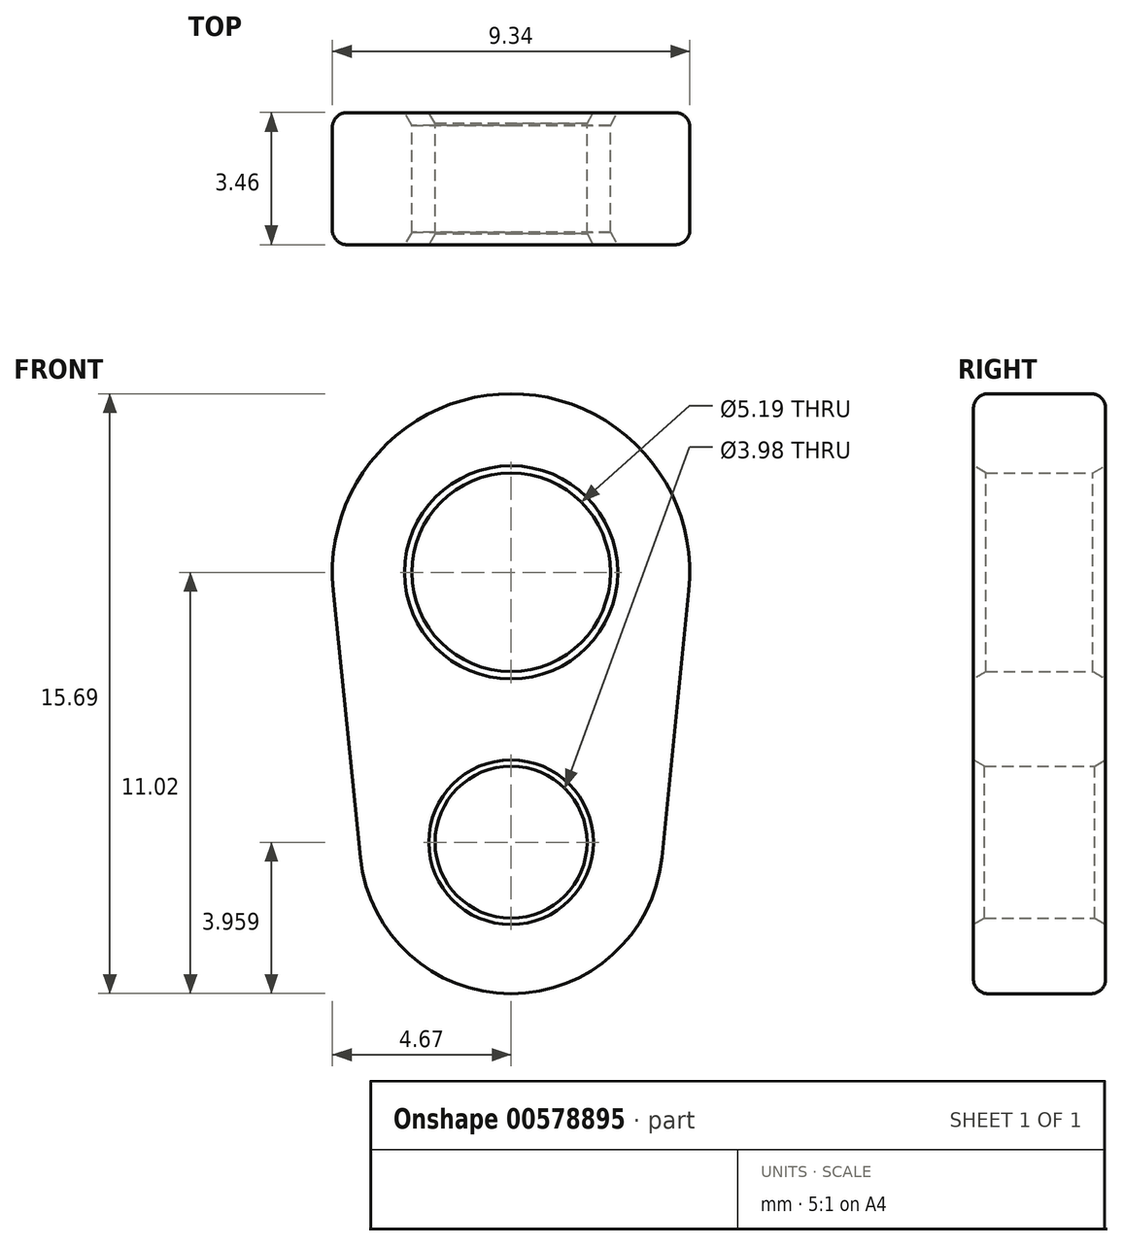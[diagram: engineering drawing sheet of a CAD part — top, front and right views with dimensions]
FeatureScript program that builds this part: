
annotation { "Feature Type Name" : "Feature", "Feature Type Description" : "" }
export const myFeature = defineFeature(function(context is Context, id is Id, definition is map)
    precondition{}
    {
        {
            var Q0;
            Q0=qCreatedBy(makeId("Front.planeOp"),FACE);
            var sketch = newSketch(context, id + "F0", { "sketchPlane" : qUnion([Q0])});
            skCircle(sketch, "E0", {"center": v(0, 0) * mm, "radius": 2.6 * mm});
            skCircle(sketch, "E1", {"center": v(0, -7.06) * mm, "radius": 1.99 * mm});
            skArc(sketch, "E2", {"start": v(-4.65, -0.47) * mm, "mid": v(0, 4.67) * mm, "end": v(4.65, -0.47) * mm});
            skArc(sketch, "E3", {"start": v(-3.94, -7.46) * mm, "mid": v(0, -11.02) * mm, "end": v(3.94, -7.46) * mm});
            skLineSegment(sketch, "E4", {"start": v(-4.65, -0.47) * mm, "end": v(-3.94, -7.46) * mm});
            skLineSegment(sketch, "E5", {"start": v(4.65, -0.47) * mm, "end": v(3.94, -7.46) * mm});
            skSolve(sketch);
        }
        {
            var Q0;
            Q0=makeQuery(id+"F0.imprint","IMPRINT",FACE,{"disambiguationData":[TD([[makeQuery(id+"F0.imprint","IMPRINT",EDGE,{"derivedFrom":sQuery(id+"F0.wireOp",EDGE,"E0")}),-1.0]])]});
            extrude(context, id + "F1", {"entities" : qUnion([Q0]), "endBound" : BoundingType.SYMMETRIC, "depth" : 3.45 * mm});
        }
        {
            var Q0;
            Q0=makeQuery(id+"F1.opExtrude","CAP_EDGE",EDGE,{"disambiguationData":[OSD([sQuery(id+"F0.wireOp",EDGE,"E5")])],"isStart":false});
            var Q1;
            Q1=makeQuery(id+"F1.opExtrude","CAP_EDGE",EDGE,{"disambiguationData":[OSD([sQuery(id+"F0.wireOp",EDGE,"E2")])],"isStart":false});
            var Q2;
            Q2=makeQuery(id+"F1.opExtrude","CAP_EDGE",EDGE,{"disambiguationData":[OSD([sQuery(id+"F0.wireOp",EDGE,"E4")])],"isStart":false});
            var Q3;
            Q3=makeQuery(id+"F1.opExtrude","CAP_EDGE",EDGE,{"disambiguationData":[OSD([sQuery(id+"F0.wireOp",EDGE,"E3")])],"isStart":false});
            fillet(context, id + "F2", {"entities" : qUnion([Q0, Q1, Q2, Q3]), "radius" : 0.38 * mm, "tangentPropagation" : true, "allowEdgeOverflow" : false});
        }
        {
            var Q0;
            Q0=makeQuery(id+"F1.opExtrude","CAP_EDGE",EDGE,{"disambiguationData":[OSD([sQuery(id+"F0.wireOp",EDGE,"E5")])],"isStart":true});
            var Q1;
            Q1=makeQuery(id+"F1.opExtrude","CAP_EDGE",EDGE,{"disambiguationData":[OSD([sQuery(id+"F0.wireOp",EDGE,"E2")])],"isStart":true});
            var Q2;
            Q2=makeQuery(id+"F1.opExtrude","CAP_EDGE",EDGE,{"disambiguationData":[OSD([sQuery(id+"F0.wireOp",EDGE,"E4")])],"isStart":true});
            var Q3;
            Q3=makeQuery(id+"F1.opExtrude","CAP_EDGE",EDGE,{"disambiguationData":[OSD([sQuery(id+"F0.wireOp",EDGE,"E3")])],"isStart":true});
            fillet(context, id + "F3", {"entities" : qUnion([Q0, Q1, Q2, Q3]), "radius" : 0.38 * mm, "tangentPropagation" : true, "allowEdgeOverflow" : false});
        }
        {
            var Q0;
            Q0=makeQuery(id+"F1.opExtrude","CAP_EDGE",EDGE,{"disambiguationData":[OSD([sQuery(id+"F0.wireOp",EDGE,"E0")])],"isStart":false});
            var Q1;
            Q1=makeQuery(id+"F1.opExtrude","CAP_EDGE",EDGE,{"disambiguationData":[OSD([sQuery(id+"F0.wireOp",EDGE,"E0")])],"isStart":true});
            chamfer(context, id + "F4", {"entities" : qUnion([Q0, Q1]), "chamferType" : ChamferType.OFFSET_ANGLE, "width" : 0.2 * mm, "oppositeDirection" : true, "angle" : 60 * degree, "tangentPropagation" : true});
        }
        {
            var Q0;
            Q0=makeQuery(id+"F1.opExtrude","CAP_EDGE",EDGE,{"disambiguationData":[OSD([sQuery(id+"F0.wireOp",EDGE,"E1")])],"isStart":false});
            var Q1;
            Q1=makeQuery(id+"F1.opExtrude","CAP_EDGE",EDGE,{"disambiguationData":[OSD([sQuery(id+"F0.wireOp",EDGE,"E1")])],"isStart":true});
            chamfer(context, id + "F5", {"entities" : qUnion([Q0, Q1]), "chamferType" : ChamferType.OFFSET_ANGLE, "width" : 0.17 * mm, "oppositeDirection" : true, "angle" : 60 * degree, "tangentPropagation" : true});
        }
    });
